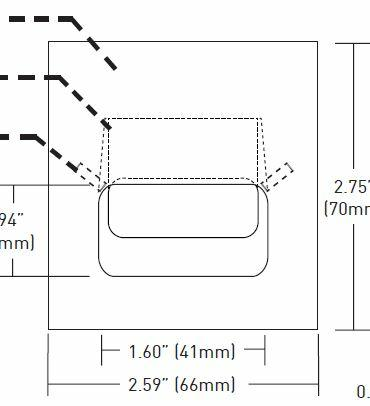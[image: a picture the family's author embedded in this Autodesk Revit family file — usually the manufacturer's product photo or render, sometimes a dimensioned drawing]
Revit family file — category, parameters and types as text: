
# Revit family: Lighting-Steplight-Lucifer-ISL1
name_source: partatom
category: Lighting Fixtures
revit_build: Autodesk Revit 2016 (Build: 20170117_1200(x64)
units: mm (PartAtom-declared; Revit-internal decimal feet)

## family parameters
Cut with Voids When Loaded = No
Host = Face
Light Source = Yes
Part Type = Normal
Room Calculation Point = No
Round Connector Dimension = Use Diameter
Shared = No

## types (1)
- Lighting-Steplight-Lucifer-ISL1
    Apparent Load = 0 VA
    Color Filter = 16777215
    Default Elevation = 4' - 0"
    Description = Steplight
    Dimming Lamp Color Temperature Shift = <None>
    Emit Shape Visible in Rendering = No
    Emit from Rectangle Length = 0' - 1 11/16"
    Emit from Rectangle Width = 0' - 1 11/16"
    Lamp = LED
    Length = 0' - 2 19/32"
    Manufacturer = Lucifer Lighting
    Model = ISL1
    Number of Poles = 1
    Photometric Web File = Load File
    Power Factor = 1
    Tilt Angle = -90.00°
    URL = http://www.luciferlighting.com
    Voltage = 0 V
    Width = 0' - 4 9/32"

## geometry (parser evidence)
native form markers: Sweep x3
no freeform markers — native parametric forms only
